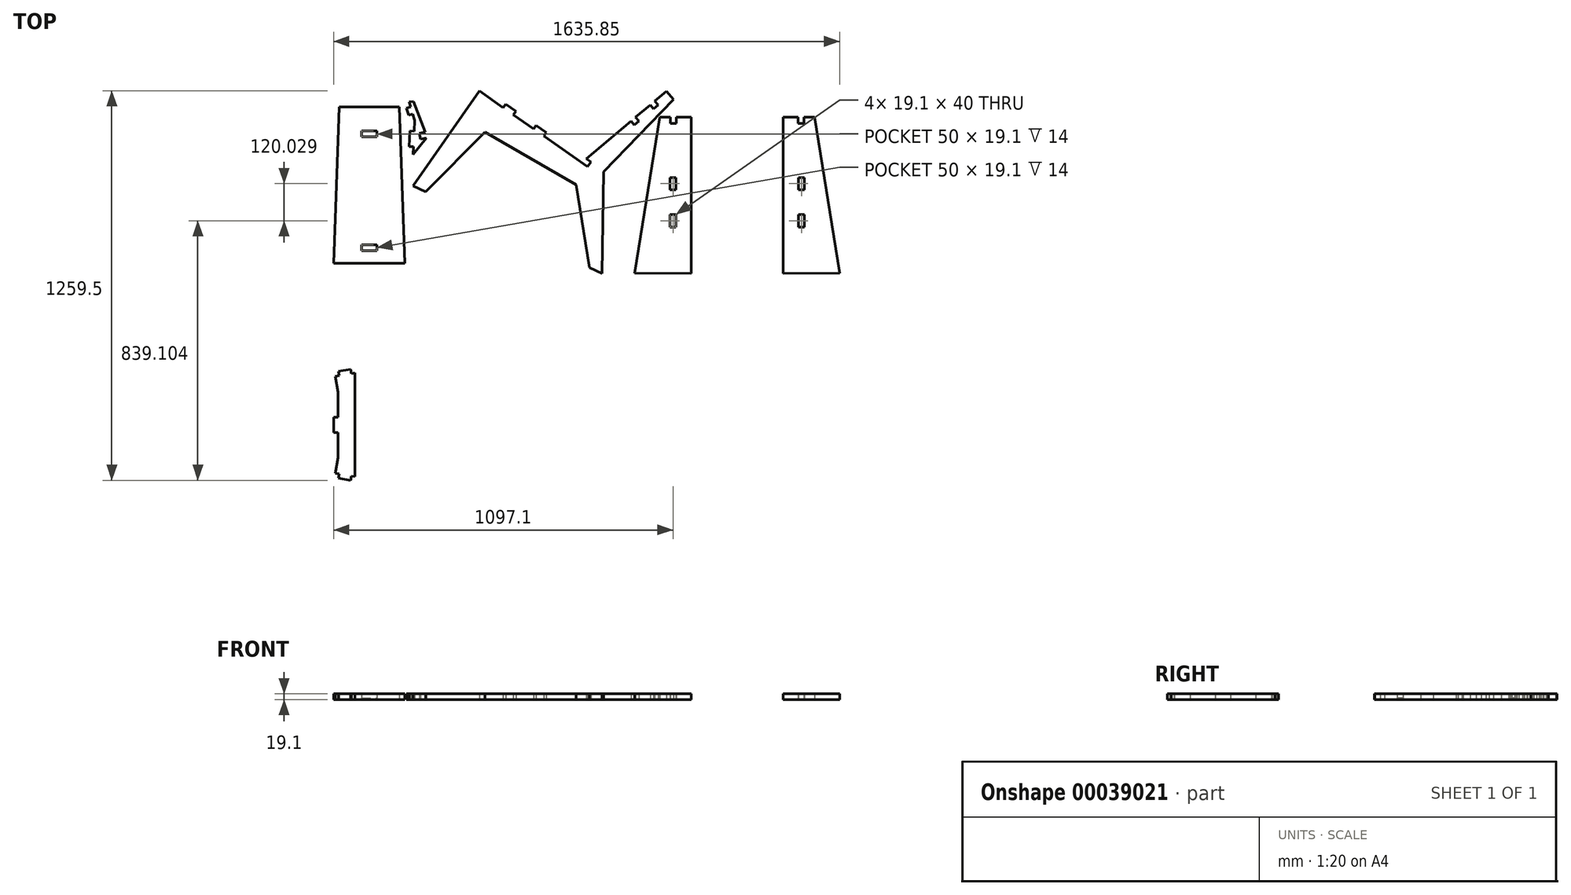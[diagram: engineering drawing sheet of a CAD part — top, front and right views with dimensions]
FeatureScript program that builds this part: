
annotation { "Feature Type Name" : "Feature", "Feature Type Description" : "" }
export const myFeature = defineFeature(function(context is Context, id is Id, definition is map)
    precondition{}
    {
        {
            assignVariable(context, id + "F0", {"name" : "materialdicke", "anyValue" : 19.1});
        }
        {
            assignVariable(context, id + "F1", {"name" : "pockettiefe", "anyValue" : 14});
        }
        {
            var Q0;
            Q0=qCreatedBy(makeId("Top.planeOp"),FACE);
            var sketch = newSketch(context, id + "F2", { "sketchPlane" : qUnion([Q0])});
            skLineSegment(sketch, "E0", {"start": v(-568.05, -822.47) * mm, "end": v(-555.84, -824.59) * mm});
            skLineSegment(sketch, "E1", {"start": v(-568.05, -822.47) * mm, "end": v(-559.22, -771.54) * mm});
            skLineSegment(sketch, "E2", {"start": v(-559.22, -771.54) * mm, "end": v(-559.22, -690.83) * mm});
            skLineSegment(sketch, "E3", {"start": v(-559.22, -690.83) * mm, "end": v(-573.22, -690.83) * mm});
            skLineSegment(sketch, "E4", {"start": v(-573.22, -665.83) * mm, "end": v(-504.22, -665.83) * mm, "construction": true});
            skLineSegment(sketch, "E5", {"start": v(-573.22, -665.83) * mm, "end": v(-573.22, -690.83) * mm});
            skLineSegment(sketch, "E6", {"start": v(-516.43, -831.43) * mm, "end": v(-504.22, -833.55) * mm});
            skLineSegment(sketch, "E7", {"start": v(-504.22, -665.83) * mm, "end": v(-504.22, -833.55) * mm});
            skLineSegment(sketch, "E8", {"start": v(-555.84, -824.59) * mm, "end": v(-558.23, -838.38) * mm});
            skLineSegment(sketch, "E9", {"start": v(-558.23, -838.38) * mm, "end": v(-518.82, -845.23) * mm});
            skLineSegment(sketch, "E10", {"start": v(-518.82, -845.23) * mm, "end": v(-516.43, -831.43) * mm});
            skLineSegment(sketch, "E11.MirrorCS", {"start": v(-516.43, -500.22) * mm, "end": v(-504.22, -498.1) * mm});
            skLineSegment(sketch, "E12.MirrorCS", {"start": v(-568.05, -509.19) * mm, "end": v(-555.84, -507.07) * mm});
            skLineSegment(sketch, "E13.MirrorCS", {"start": v(-555.84, -507.07) * mm, "end": v(-558.23, -493.27) * mm});
            skLineSegment(sketch, "E14.MirrorCS", {"start": v(-518.82, -486.43) * mm, "end": v(-516.43, -500.22) * mm});
            skLineSegment(sketch, "E15.MirrorCS", {"start": v(-559.22, -640.83) * mm, "end": v(-573.22, -640.83) * mm});
            skLineSegment(sketch, "E16.MirrorCS", {"start": v(-559.22, -560.12) * mm, "end": v(-559.22, -640.83) * mm});
            skLineSegment(sketch, "E17.MirrorCS", {"start": v(-504.22, -665.83) * mm, "end": v(-504.22, -498.1) * mm});
            skLineSegment(sketch, "E18.MirrorCS", {"start": v(-568.05, -509.19) * mm, "end": v(-559.22, -560.12) * mm});
            skLineSegment(sketch, "E19.MirrorCS", {"start": v(-558.23, -493.27) * mm, "end": v(-518.82, -486.43) * mm});
            skLineSegment(sketch, "E20.MirrorCS", {"start": v(-573.22, -665.83) * mm, "end": v(-573.22, -640.83) * mm});
            skLineSegment(sketch, "E21", {"start": v(-568.05, -822.47) * mm, "end": v(-504.22, -833.55) * mm, "construction": true});
            skPoint(sketch, "E22", {"position": v(-536.13, -828.01) * mm});
            skLineSegment(sketch, "E23", {"start": v(-536.13, -828.01) * mm, "end": v(-538.53, -841.8) * mm, "construction": true});
            skPoint(sketch, "E23.endSnap0", {"position": v(-538.53, -841.8) * mm});
            skSolve(sketch);
        }
        {
            var Q0;
            Q0=qCreatedBy(makeId("Top.planeOp"),FACE);
            var sketch = newSketch(context, id + "F3", { "sketchPlane" : qUnion([Q0])});
            skLineSegment(sketch, "E24", {"start": v(-51.77, -160.23) * mm, "end": v(-51.77, 89.77) * mm, "construction": true});
            skLineSegment(sketch, "E25", {"start": v(4.36, -7.44) * mm, "end": v(7.37, -26.3) * mm});
            skLineSegment(sketch, "E26", {"start": v(7.37, -26.3) * mm, "end": v(-17.04, -30.19) * mm});
            skLineSegment(sketch, "E27", {"start": v(4.36, -7.44) * mm, "end": v(-20.05, -11.33) * mm});
            skLineSegment(sketch, "E28", {"start": v(-20.05, -11.33) * mm, "end": v(-17.04, -30.19) * mm});
            skLineSegment(sketch, "E29", {"start": v(-7.31, -91.25) * mm, "end": v(17.1, -87.36) * mm});
            skLineSegment(sketch, "E30", {"start": v(17.1, -87.36) * mm, "end": v(20.1, -106.22) * mm});
            skLineSegment(sketch, "E31", {"start": v(20.1, -106.22) * mm, "end": v(-4.3, -110.11) * mm});
            skLineSegment(sketch, "E32", {"start": v(-4.3, -110.11) * mm, "end": v(-7.31, -91.25) * mm});
            skLineSegment(sketch, "E33.MirrorCS", {"start": v(-107.9, -7.44) * mm, "end": v(-110.9, -26.3) * mm});
            skLineSegment(sketch, "E34.MirrorCS", {"start": v(-120.63, -87.36) * mm, "end": v(-123.64, -106.22) * mm});
            skLineSegment(sketch, "E35.MirrorCS", {"start": v(-99.23, -110.11) * mm, "end": v(-96.22, -91.25) * mm});
            skLineSegment(sketch, "E36.MirrorCS", {"start": v(-83.49, -11.33) * mm, "end": v(-86.5, -30.19) * mm});
            skLineSegment(sketch, "E37.MirrorCS", {"start": v(-123.64, -106.22) * mm, "end": v(-99.23, -110.11) * mm});
            skLineSegment(sketch, "E38.MirrorCS", {"start": v(-110.9, -26.3) * mm, "end": v(-86.5, -30.19) * mm});
            skLineSegment(sketch, "E39.MirrorCS", {"start": v(-107.9, -7.44) * mm, "end": v(-83.49, -11.33) * mm});
            skLineSegment(sketch, "E40.MirrorCS", {"start": v(-96.22, -91.25) * mm, "end": v(-120.63, -87.36) * mm});
            skLineSegment(sketch, "E41", {"start": v(-18.54, -20.76) * mm, "end": v(-51.77, -26.05) * mm, "construction": true});
            skLineSegment(sketch, "E42", {"start": v(-18.54, -20.76) * mm, "end": v(-5.81, -100.68) * mm, "construction": true});
            skPoint(sketch, "E42.endSnap0", {"position": v(-5.81, -100.68) * mm});
            skLineSegment(sketch, "E43", {"start": v(-103.4, 89.77) * mm, "end": v(-0.13, 89.77) * mm, "construction": true});
            skLineSegment(sketch, "E44", {"start": v(43.95, -160.23) * mm, "end": v(-147.48, -160.23) * mm, "construction": true});
            skFitSpline(sketch, "E45", {"points": [v(-51.77, 89.77) * mm, v(-6.4, 88.76) * mm, v(0.43, 86.63) * mm], "startDerivative": vector(77.46, 0.74) * mm, "endDerivative": vector(18.44, -8.34) * mm});
            skFitSpline(sketch, "E46.MirrorCS", {"points": [v(-51.77, 89.77) * mm, v(-97.14, 88.76) * mm, v(-103.96, 86.63) * mm], "startDerivative": vector(-77.46, 0.74) * mm, "endDerivative": vector(-18.44, -8.34) * mm});
            skFitSpline(sketch, "E47", {"points": [v(-51.77, -160.23) * mm, v(31.02, -157.68) * mm, v(43.17, -155.8) * mm], "startDerivative": vector(140.31, 2.36) * mm, "endDerivative": vector(28.68, 7.15) * mm});
            skFitSpline(sketch, "E48.MirrorCS", {"points": [v(-51.77, -160.23) * mm, v(-134.56, -157.68) * mm, v(-146.7, -155.8) * mm], "startDerivative": vector(-140.31, 2.36) * mm, "endDerivative": vector(-28.68, 7.15) * mm});
            skFitSpline(sketch, "E49", {"points": [v(192.8, -135.68) * mm, v(175.44, -145.74) * mm, v(-51.77, -160.23) * mm], "startDerivative": vector(-50.76, -46.81) * mm, "endDerivative": vector(-379.02, -9.09) * mm, "construction": true});
            skLineSegment(sketch, "E50", {"start": v(43.17, -155.8) * mm, "end": v(-0.13, 89.77) * mm});
            skLineSegment(sketch, "E51.MirrorCS", {"start": v(-146.7, -155.8) * mm, "end": v(-103.4, 89.77) * mm});
            skFitSpline(sketch, "E52.MirrorCS", {"points": [v(-296.33, -135.68) * mm, v(-278.98, -145.74) * mm, v(-51.77, -160.23) * mm], "startDerivative": vector(50.76, -46.81) * mm, "endDerivative": vector(379.02, -9.09) * mm, "construction": true});
            skLineSegment(sketch, "E53", {"start": v(-146.7, -155.8) * mm, "end": v(-147.02, -157.6) * mm});
            skSolve(sketch);
        }
        {
            var Q0;
            Q0=qCreatedBy(makeId("Top.planeOp"),FACE);
            var sketch = newSketch(context, id + "F4", { "sketchPlane" : qUnion([Q0])});
            skLineSegment(sketch, "E54", {"start": v(-327.11, 284.24) * mm, "end": v(-329.17, 234.28) * mm});
            skLineSegment(sketch, "E55", {"start": v(-329.17, 234.28) * mm, "end": v(-315.19, 233.7) * mm});
            skLineSegment(sketch, "E56", {"start": v(-315.19, 233.7) * mm, "end": v(-316.22, 208.73) * mm});
            skLineSegment(sketch, "E57", {"start": v(-316.22, 208.73) * mm, "end": v(-273.3, 262.22) * mm});
            skLineSegment(sketch, "E58", {"start": v(-273.3, 262.22) * mm, "end": v(-292.34, 258.02) * mm});
            skLineSegment(sketch, "E59", {"start": v(-292.34, 258.02) * mm, "end": v(-296.45, 276.68) * mm});
            skLineSegment(sketch, "E60", {"start": v(-296.45, 276.68) * mm, "end": v(-277.41, 280.87) * mm});
            skLineSegment(sketch, "E61", {"start": v(-277.41, 280.87) * mm, "end": v(-315.94, 380) * mm});
            skLineSegment(sketch, "E62", {"start": v(-315.94, 380) * mm, "end": v(-329.58, 378.23) * mm});
            skLineSegment(sketch, "E63", {"start": v(-329.58, 378.23) * mm, "end": v(-324.87, 362.47) * mm});
            skLineSegment(sketch, "E64", {"start": v(-324.87, 362.47) * mm, "end": v(-338.29, 358.46) * mm});
            skLineSegment(sketch, "E65", {"start": v(-338.29, 358.46) * mm, "end": v(-331.2, 334.78) * mm});
            skLineSegment(sketch, "E66", {"start": v(-331.2, 334.78) * mm, "end": v(-317.8, 338.8) * mm});
            skLineSegment(sketch, "E67", {"start": v(-317.8, 338.8) * mm, "end": v(-311.7, 318.38) * mm});
            skLineSegment(sketch, "E68", {"start": v(-311.7, 318.38) * mm, "end": v(-313.13, 283.66) * mm});
            skLineSegment(sketch, "E69", {"start": v(-313.13, 283.66) * mm, "end": v(-327.11, 284.24) * mm});
            skSolve(sketch);
        }
        {
            var Q0;
            Q0=qCreatedBy(makeId("Top.planeOp"),FACE);
            var sketch = newSketch(context, id + "F5", { "sketchPlane" : qUnion([Q0])});
            skLineSegment(sketch, "E70", {"start": v(-556.1, 361.7) * mm, "end": v(-361.38, 361.7) * mm});
            skLineSegment(sketch, "E71", {"start": v(-361.38, 361.7) * mm, "end": v(-343.74, -143.3) * mm});
            skLineSegment(sketch, "E72", {"start": v(-343.74, -143.3) * mm, "end": v(-573.74, -143.3) * mm});
            skLineSegment(sketch, "E73", {"start": v(-573.74, -143.3) * mm, "end": v(-556.1, 361.7) * mm});
            skLineSegment(sketch, "E74", {"start": v(-458.74, 274.96) * mm, "end": v(-458.74, -93.15) * mm, "construction": true});
            skPoint(sketch, "E75", {"position": v(-458.74, 361.7) * mm});
            skLineSegment(sketch, "E76.rect.bottom", {"start": v(-483.74, 284.5) * mm, "end": v(-433.74, 284.5) * mm});
            skLineSegment(sketch, "E76.rect.top", {"start": v(-483.74, 265.4) * mm, "end": v(-433.74, 265.4) * mm});
            skLineSegment(sketch, "E76.rect.left", {"start": v(-483.74, 284.5) * mm, "end": v(-483.74, 265.4) * mm});
            skLineSegment(sketch, "E76.rect.right", {"start": v(-433.74, 284.5) * mm, "end": v(-433.74, 265.4) * mm});
            skPoint(sketch, "E76.rect.middle", {"position": v(-458.74, 274.96) * mm});
            skLineSegment(sketch, "E77.rect.bottom", {"start": v(-483.74, -83.6) * mm, "end": v(-433.74, -83.6) * mm});
            skLineSegment(sketch, "E77.rect.top", {"start": v(-483.74, -102.7) * mm, "end": v(-433.74, -102.7) * mm});
            skLineSegment(sketch, "E77.rect.left", {"start": v(-483.74, -83.6) * mm, "end": v(-483.74, -102.7) * mm});
            skLineSegment(sketch, "E77.rect.right", {"start": v(-433.74, -83.6) * mm, "end": v(-433.74, -102.7) * mm});
            skPoint(sketch, "E77.rect.middle", {"position": v(-458.74, -93.15) * mm});
            skLineSegment(sketch, "E78", {"start": v(-458.74, 361.7) * mm, "end": v(-458.74, 284.5) * mm, "construction": true});
            skSolve(sketch);
        }
        {
            var Q0;
            Q0=qCreatedBy(makeId("Top.planeOp"),FACE);
            var sketch = newSketch(context, id + "F6", { "sketchPlane" : qUnion([Q0])});
            skLineSegment(sketch, "E79", {"start": v(-317, 106.93) * mm, "end": v(-102.66, 414.27) * mm});
            skLineSegment(sketch, "E80", {"start": v(-102.66, 414.27) * mm, "end": v(-25.32, 359.95) * mm});
            skLineSegment(sketch, "E81", {"start": v(228.31, 181.79) * mm, "end": v(243.42, 194.51) * mm, "construction": true});
            skLineSegment(sketch, "E82", {"start": v(502.65, 412.84) * mm, "end": v(524.65, 386.72) * mm});
            skLineSegment(sketch, "E83", {"start": v(524.65, 386.72) * mm, "end": v(299.53, 152.48) * mm});
            skLineSegment(sketch, "E84", {"start": v(299.53, 152.48) * mm, "end": v(294.4, -176.78) * mm});
            skLineSegment(sketch, "E85", {"start": v(294.4, -176.78) * mm, "end": v(253.58, -157.83) * mm});
            skLineSegment(sketch, "E86", {"start": v(253.58, -157.83) * mm, "end": v(210.46, 111.14) * mm});
            skLineSegment(sketch, "E87", {"start": v(210.46, 111.14) * mm, "end": v(-84.3, 280.6) * mm});
            skLineSegment(sketch, "E88", {"start": v(-84.3, 280.6) * mm, "end": v(-276.18, 87.99) * mm});
            skLineSegment(sketch, "E89", {"start": v(-276.18, 87.99) * mm, "end": v(-317, 106.93) * mm});
            skLineSegment(sketch, "E90", {"start": v(-25.32, 359.95) * mm, "end": v(-17.27, 371.4) * mm});
            skLineSegment(sketch, "E91", {"start": v(-17.27, 371.4) * mm, "end": v(15.46, 348.41) * mm});
            skLineSegment(sketch, "E92", {"start": v(15.46, 348.41) * mm, "end": v(7.4, 336.96) * mm});
            skLineSegment(sketch, "E93", {"start": v(72.87, 290.97) * mm, "end": v(80.92, 302.43) * mm});
            skLineSegment(sketch, "E94", {"start": v(80.92, 302.43) * mm, "end": v(113.65, 279.44) * mm});
            skLineSegment(sketch, "E95", {"start": v(113.65, 279.44) * mm, "end": v(105.6, 267.98) * mm});
            skLineSegment(sketch, "E96", {"start": v(243.42, 194.51) * mm, "end": v(258.17, 184.16) * mm});
            skLineSegment(sketch, "E97", {"start": v(258.17, 184.16) * mm, "end": v(247.19, 168.53) * mm});
            skLineSegment(sketch, "E98", {"start": v(247.19, 168.53) * mm, "end": v(228.31, 181.79) * mm});
            skLineSegment(sketch, "E99", {"start": v(243.42, 194.51) * mm, "end": v(387.95, 316.24) * mm});
            skLineSegment(sketch, "E100", {"start": v(72.87, 290.97) * mm, "end": v(105.6, 267.98) * mm, "construction": true});
            skLineSegment(sketch, "E101", {"start": v(105.6, 267.98) * mm, "end": v(228.31, 181.79) * mm});
            skLineSegment(sketch, "E102", {"start": v(-25.32, 359.95) * mm, "end": v(7.4, 336.96) * mm, "construction": true});
            skLineSegment(sketch, "E103", {"start": v(7.4, 336.96) * mm, "end": v(72.87, 290.97) * mm});
            skLineSegment(sketch, "E104", {"start": v(387.95, 316.24) * mm, "end": v(398.57, 303.63) * mm});
            skLineSegment(sketch, "E105", {"start": v(398.57, 303.63) * mm, "end": v(413.18, 315.93) * mm});
            skLineSegment(sketch, "E106", {"start": v(413.18, 315.93) * mm, "end": v(402.56, 328.54) * mm});
            skLineSegment(sketch, "E107", {"start": v(402.56, 328.54) * mm, "end": v(449.83, 368.35) * mm});
            skLineSegment(sketch, "E108", {"start": v(387.95, 316.24) * mm, "end": v(402.56, 328.54) * mm, "construction": true});
            skLineSegment(sketch, "E109", {"start": v(449.83, 368.35) * mm, "end": v(460.45, 355.74) * mm});
            skLineSegment(sketch, "E110", {"start": v(460.45, 355.74) * mm, "end": v(475.06, 368.04) * mm});
            skLineSegment(sketch, "E111", {"start": v(475.06, 368.04) * mm, "end": v(464.43, 380.66) * mm});
            skLineSegment(sketch, "E112", {"start": v(464.43, 380.66) * mm, "end": v(502.65, 412.84) * mm});
            skLineSegment(sketch, "E113", {"start": v(449.83, 368.35) * mm, "end": v(464.43, 380.66) * mm, "construction": true});
            skPoint(sketch, "E114", {"position": v(405.88, 309.78) * mm});
            skPoint(sketch, "E115", {"position": v(467.75, 361.9) * mm});
            skLineSegment(sketch, "E116", {"start": v(-388.66, -240.51) * mm, "end": v(695.72, -240.51) * mm, "construction": true});
            skLineSegment(sketch, "E117.MirrorCS", {"start": v(228.31, -662.81) * mm, "end": v(243.42, -675.54) * mm, "construction": true});
            skLineSegment(sketch, "E118.MirrorCS", {"start": v(449.83, -849.38) * mm, "end": v(464.43, -861.68) * mm, "construction": true});
            skLineSegment(sketch, "E119.MirrorCS", {"start": v(258.17, -665.18) * mm, "end": v(247.19, -649.55) * mm});
            skLineSegment(sketch, "E120.MirrorCS", {"start": v(72.87, -772) * mm, "end": v(105.6, -749) * mm, "construction": true});
            skLineSegment(sketch, "E121.MirrorCS", {"start": v(7.4, -817.98) * mm, "end": v(72.87, -772) * mm});
            skLineSegment(sketch, "E122.MirrorCS", {"start": v(247.19, -649.55) * mm, "end": v(228.31, -662.81) * mm});
            skLineSegment(sketch, "E123.MirrorCS", {"start": v(-25.32, -840.97) * mm, "end": v(7.4, -817.98) * mm, "construction": true});
            skLineSegment(sketch, "E124.MirrorCS", {"start": v(72.87, -772) * mm, "end": v(80.92, -783.45) * mm});
            skLineSegment(sketch, "E125.MirrorCS", {"start": v(243.42, -675.54) * mm, "end": v(258.17, -665.18) * mm});
            skLineSegment(sketch, "E126.MirrorCS", {"start": v(449.83, -849.38) * mm, "end": v(460.45, -836.76) * mm});
            skLineSegment(sketch, "E127.MirrorCS", {"start": v(460.45, -836.76) * mm, "end": v(475.06, -849.07) * mm});
            skLineSegment(sketch, "E128.MirrorCS", {"start": v(-25.32, -840.97) * mm, "end": v(-17.27, -852.43) * mm});
            skLineSegment(sketch, "E129.MirrorCS", {"start": v(-17.27, -852.43) * mm, "end": v(15.46, -829.44) * mm});
            skLineSegment(sketch, "E130.MirrorCS", {"start": v(113.65, -760.46) * mm, "end": v(105.6, -749) * mm});
            skLineSegment(sketch, "E131.MirrorCS", {"start": v(475.06, -849.07) * mm, "end": v(464.43, -861.68) * mm});
            skLineSegment(sketch, "E132.MirrorCS", {"start": v(15.46, -829.44) * mm, "end": v(7.4, -817.98) * mm});
            skLineSegment(sketch, "E133.MirrorCS", {"start": v(80.92, -783.45) * mm, "end": v(113.65, -760.46) * mm});
            skLineSegment(sketch, "E134.MirrorCS", {"start": v(398.57, -784.65) * mm, "end": v(413.18, -796.95) * mm});
            skLineSegment(sketch, "E135.MirrorCS", {"start": v(402.56, -809.57) * mm, "end": v(449.83, -849.38) * mm});
            skLineSegment(sketch, "E136.MirrorCS", {"start": v(387.95, -797.26) * mm, "end": v(398.57, -784.65) * mm});
            skLineSegment(sketch, "E137.MirrorCS", {"start": v(413.18, -796.95) * mm, "end": v(402.56, -809.57) * mm});
            skLineSegment(sketch, "E138.MirrorCS", {"start": v(387.95, -797.26) * mm, "end": v(402.56, -809.57) * mm, "construction": true});
            skLineSegment(sketch, "E139.MirrorCS", {"start": v(294.4, -304.25) * mm, "end": v(253.58, -323.2) * mm});
            skLineSegment(sketch, "E140.MirrorCS", {"start": v(464.43, -861.68) * mm, "end": v(502.65, -893.87) * mm});
            skLineSegment(sketch, "E141.MirrorCS", {"start": v(-276.18, -569.01) * mm, "end": v(-317, -587.95) * mm});
            skLineSegment(sketch, "E142.MirrorCS", {"start": v(502.65, -893.87) * mm, "end": v(524.65, -867.74) * mm});
            skLineSegment(sketch, "E143.MirrorCS", {"start": v(-102.66, -895.3) * mm, "end": v(-25.32, -840.97) * mm});
            skLineSegment(sketch, "E144.MirrorCS", {"start": v(105.6, -749) * mm, "end": v(228.31, -662.81) * mm});
            skLineSegment(sketch, "E145.MirrorCS", {"start": v(524.65, -867.74) * mm, "end": v(299.53, -633.5) * mm});
            skPoint(sketch, "E146.MirrorP", {"position": v(405.88, -790.8) * mm});
            skPoint(sketch, "E147.MirrorP", {"position": v(467.75, -842.92) * mm});
            skLineSegment(sketch, "E148.MirrorCS", {"start": v(253.58, -323.2) * mm, "end": v(210.46, -592.17) * mm});
            skLineSegment(sketch, "E149.MirrorCS", {"start": v(210.46, -592.17) * mm, "end": v(-84.3, -761.61) * mm});
            skLineSegment(sketch, "E150.MirrorCS", {"start": v(299.53, -633.5) * mm, "end": v(294.4, -304.25) * mm});
            skLineSegment(sketch, "E151.MirrorCS", {"start": v(-84.3, -761.61) * mm, "end": v(-276.18, -569.01) * mm});
            skLineSegment(sketch, "E152.MirrorCS", {"start": v(243.42, -675.54) * mm, "end": v(387.95, -797.26) * mm});
            skLineSegment(sketch, "E153.MirrorCS", {"start": v(-317, -587.95) * mm, "end": v(-102.66, -895.3) * mm});
            skSolve(sketch);
        }
        {
            var Q0;
            Q0=qCreatedBy(makeId("Top.planeOp"),FACE);
            var sketch = newSketch(context, id + "F7", { "sketchPlane" : qUnion([Q0])});
            skLineSegment(sketch, "E154", {"start": v(582, 328.99) * mm, "end": v(582, -176.3) * mm});
            skLineSegment(sketch, "E155", {"start": v(582, -176.3) * mm, "end": v(399.95, -175.54) * mm});
            skLineSegment(sketch, "E156", {"start": v(399.95, -175.54) * mm, "end": v(480.75, 329.41) * mm});
            skLineSegment(sketch, "E157", {"start": v(480.75, 329.41) * mm, "end": v(514.7, 329.27) * mm});
            skLineSegment(sketch, "E158", {"start": v(513.81, 133.9) * mm, "end": v(532.91, 133.9) * mm});
            skLineSegment(sketch, "E159", {"start": v(532.91, 133.9) * mm, "end": v(532.91, 93.9) * mm});
            skLineSegment(sketch, "E160", {"start": v(532.91, 93.9) * mm, "end": v(513.81, 93.9) * mm});
            skLineSegment(sketch, "E161", {"start": v(513.81, 93.9) * mm, "end": v(513.81, 133.9) * mm});
            skLineSegment(sketch, "E162", {"start": v(514.7, 329.27) * mm, "end": v(514.6, 308.72) * mm});
            skLineSegment(sketch, "E163", {"start": v(514.6, 308.72) * mm, "end": v(533.7, 308.64) * mm});
            skLineSegment(sketch, "E164", {"start": v(514.7, 329.27) * mm, "end": v(533.8, 329.2) * mm, "construction": true});
            skLineSegment(sketch, "E165", {"start": v(533.7, 308.64) * mm, "end": v(533.8, 329.2) * mm});
            skLineSegment(sketch, "E166", {"start": v(533.8, 329.2) * mm, "end": v(582, 328.99) * mm});
            skLineSegment(sketch, "E167", {"start": v(513.81, 13.87) * mm, "end": v(532.91, 13.87) * mm});
            skLineSegment(sketch, "E168", {"start": v(532.91, 13.87) * mm, "end": v(532.91, -26.13) * mm});
            skLineSegment(sketch, "E169", {"start": v(532.91, -26.13) * mm, "end": v(513.81, -26.13) * mm});
            skLineSegment(sketch, "E170", {"start": v(513.81, -26.13) * mm, "end": v(513.81, 13.87) * mm});
            skLineSegment(sketch, "E171", {"start": v(523.36, 133.9) * mm, "end": v(524.16, 308.68) * mm, "construction": true});
            skLineSegment(sketch, "E172", {"start": v(523.62, 190.1) * mm, "end": v(582, 189.84) * mm, "construction": true});
            skLineSegment(sketch, "E173", {"start": v(523.36, 133.9) * mm, "end": v(523.36, 13.87) * mm, "construction": true});
            skLineSegment(sketch, "E174", {"start": v(731.03, 365.82) * mm, "end": v(731.03, -223.19) * mm, "construction": true});
            skLineSegment(sketch, "E175.MirrorCS", {"start": v(948.25, 13.87) * mm, "end": v(929.15, 13.87) * mm});
            skLineSegment(sketch, "E176.MirrorCS", {"start": v(948.25, 133.9) * mm, "end": v(929.15, 133.9) * mm});
            skLineSegment(sketch, "E177.MirrorCS", {"start": v(929.15, 93.9) * mm, "end": v(948.25, 93.9) * mm});
            skLineSegment(sketch, "E178.MirrorCS", {"start": v(928.36, 308.64) * mm, "end": v(928.27, 329.2) * mm});
            skLineSegment(sketch, "E179.MirrorCS", {"start": v(947.46, 308.72) * mm, "end": v(928.36, 308.64) * mm});
            skLineSegment(sketch, "E180.MirrorCS", {"start": v(947.37, 329.27) * mm, "end": v(947.46, 308.72) * mm});
            skLineSegment(sketch, "E181.MirrorCS", {"start": v(929.15, -26.13) * mm, "end": v(948.25, -26.13) * mm});
            skLineSegment(sketch, "E182.MirrorCS", {"start": v(929.15, 133.9) * mm, "end": v(929.15, 93.9) * mm});
            skLineSegment(sketch, "E183.MirrorCS", {"start": v(929.15, 13.87) * mm, "end": v(929.15, -26.13) * mm});
            skLineSegment(sketch, "E184.MirrorCS", {"start": v(981.32, 329.41) * mm, "end": v(947.37, 329.27) * mm});
            skLineSegment(sketch, "E185.MirrorCS", {"start": v(928.27, 329.2) * mm, "end": v(880.06, 328.99) * mm});
            skLineSegment(sketch, "E186.MirrorCS", {"start": v(880.06, 328.99) * mm, "end": v(880.06, -176.3) * mm});
            skLineSegment(sketch, "E187.MirrorCS", {"start": v(948.25, 93.9) * mm, "end": v(948.25, 133.9) * mm});
            skLineSegment(sketch, "E188.MirrorCS", {"start": v(948.25, -26.13) * mm, "end": v(948.25, 13.87) * mm});
            skLineSegment(sketch, "E189.MirrorCS", {"start": v(1062.11, -175.54) * mm, "end": v(981.32, 329.41) * mm});
            skLineSegment(sketch, "E190.MirrorCS", {"start": v(880.06, -176.3) * mm, "end": v(1062.11, -175.54) * mm});
            skSolve(sketch);
        }
        {
            var Q0;
            Q0=makeQuery(id+"F4.imprint","IMPRINT",FACE,{"disambiguationData":[TD([[makeQuery(id+"F4.imprint","IMPRINT",EDGE,{"derivedFrom":sQuery(id+"F4.wireOp",EDGE,"E54")}),1.0]])]});
            extrude(context, id + "F8", {"entities" : qUnion([Q0]), "depth" : (getVariable(context, 'materialdicke')) * mm});
        }
        {
            var Q0;
            Q0=makeQuery(id+"F5.imprint","IMPRINT",FACE,{"disambiguationData":[TD([[makeQuery(id+"F5.imprint","IMPRINT",EDGE,{"derivedFrom":sQuery(id+"F5.wireOp",EDGE,"E70")}),-1.0]])]});
            extrude(context, id + "F9", {"entities" : qUnion([Q0]), "depth" : (getVariable(context, 'materialdicke')) * mm});
        }
        {
            var Q0;
            Q0=makeQuery(id+"F5.imprint","IMPRINT",FACE,{"disambiguationData":[TD([[makeQuery(id+"F5.imprint","IMPRINT",EDGE,{"derivedFrom":sQuery(id+"F5.wireOp",EDGE,"E76.rect.bottom")}),-1.0]])]});
            var Q1;
            Q1=makeQuery(id+"F5.imprint","IMPRINT",FACE,{"disambiguationData":[TD([[makeQuery(id+"F5.imprint","IMPRINT",EDGE,{"derivedFrom":sQuery(id+"F5.wireOp",EDGE,"E77.rect.bottom")}),-1.0]])]});
            extrude(context, id + "F10", {"entities" : qUnion([Q0, Q1]), "operationType" : NewBodyOperationType.ADD, "depth" : (getVariable(context, 'materialdicke') - getVariable(context, 'pockettiefe')) * mm});
        }
        {
            var Q0;
            Q0=makeQuery(id+"F7.imprint","IMPRINT",FACE,{"disambiguationData":[TD([[makeQuery(id+"F7.imprint","IMPRINT",EDGE,{"derivedFrom":sQuery(id+"F7.wireOp",EDGE,"E154")}),-1.0]])]});
            extrude(context, id + "F11", {"entities" : qUnion([Q0]), "depth" : (getVariable(context, 'materialdicke')) * mm});
        }
        {
            var Q0;
            Q0=makeQuery(id+"F7.imprint","IMPRINT",FACE,{"disambiguationData":[TD([[makeQuery(id+"F7.imprint","IMPRINT",EDGE,{"derivedFrom":sQuery(id+"F7.wireOp",EDGE,"E175.MirrorCS")}),-1.0]])]});
            extrude(context, id + "F12", {"entities" : qUnion([Q0]), "depth" : (getVariable(context, 'materialdicke')) * mm});
        }
        {
            var Q0;
            Q0=makeQuery(id+"F6.imprint","IMPRINT",FACE,{"disambiguationData":[TD([[makeQuery(id+"F6.imprint","IMPRINT",EDGE,{"derivedFrom":sQuery(id+"F6.wireOp",EDGE,"E79")}),-1.0]])]});
            extrude(context, id + "F13", {"entities" : qUnion([Q0]), "depth" : (getVariable(context, 'materialdicke')) * mm});
        }
        {
            var Q0;
            Q0=makeQuery(id+"F2.imprint","IMPRINT",FACE,{"disambiguationData":[TD([[makeQuery(id+"F2.imprint","IMPRINT",EDGE,{"derivedFrom":sQuery(id+"F2.wireOp",EDGE,"E0")}),1.0]])]});
            extrude(context, id + "F14", {"entities" : qUnion([Q0]), "depth" : (getVariable(context, 'materialdicke')) * mm});
        }
    });
